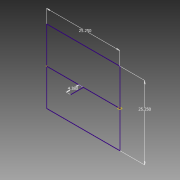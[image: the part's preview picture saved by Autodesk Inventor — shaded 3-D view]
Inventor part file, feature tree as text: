
AUTODESK INVENTOR PART (.ipt)
format: ipt  version: 2013 (Build 170138000, 138)  size: 65,024 bytes
history: native  units: in
note: dims shown in document units (in); Inventor stores cm internally (conversion verified against a paired STEP export)
features: sketch x2, plane x1
ambient origin geometry x8: Origin, YZ Plane, XZ Plane, XY Plane, X Axis, Y Axis, Z Axis, Center Point
feature tree (3):
  sketch  "Sketch1"  dims[d0=25.25in]
  plane  "Work Plane1"
  sketch  "Sketch2"  dims[d1=25.25in d2=4.38in]
